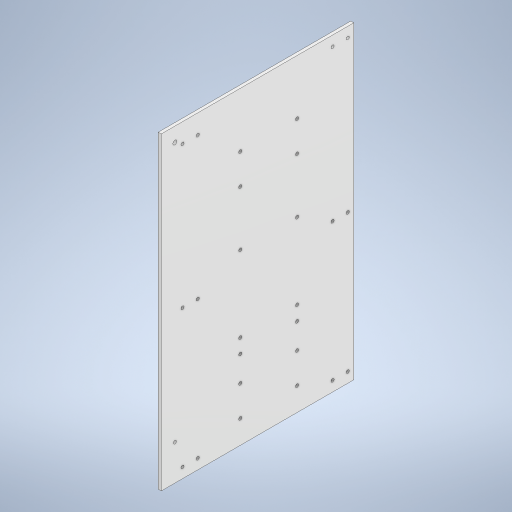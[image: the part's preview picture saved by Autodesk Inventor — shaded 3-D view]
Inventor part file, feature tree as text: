
AUTODESK INVENTOR PART (.ipt)
format: ipt  version: 2024.3 (Build 283343000, 343)  size: 461,824 bytes
history: native  units: mm
features: extrude x17, sketch x17, other x1, projected_geometry x1
ambient origin geometry x8: Origin, YZ Plane, XZ Plane, XY Plane, X Axis, Y Axis, Z Axis, Center Point
bodies: Body1 (feature_tree)
feature tree (36):
  other  "ソリッド1"
  extrude  "押し出し1"  Depth=150.0mm
  extrude  "押し出し2"  Depth=175.0mm
  sketch  "スケッチ3"
  extrude  "押し出し4"  Depth=3.0mm TaperAngle=0.0deg
  extrude  "押し出し5"  Depth=3.0mm
  extrude  "押し出し7"  Depth=6.0mm
  extrude  "押し出し8"  Depth=15.0mm
  extrude  "押し出し9"  Depth=3.0mm
  extrude  "押し出し10"  TaperAngle=0.0deg  [1 undecoded]
  extrude  "押し出し11"  Depth=6.0mm
  extrude  "押し出し12"  Depth=3.0mm
  extrude  "押し出し13"  Depth=15.0mm
  extrude  "押し出し14"  Depth=3.0mm
  extrude  "押し出し15"  Depth=3.0mm
  extrude  "押し出し16"  Depth=3.0mm
  extrude  "押し出し17"  Depth=6.0mm
  extrude  "押し出し18"  Depth=15.0mm
  extrude  "押し出し19"  Depth=5.0mm
  sketch  "スケッチ1"
  sketch  "スケッチ2"
  sketch  "スケッチ6"
  sketch  "スケッチ7"
  sketch  "スケッチ9"
  sketch  "スケッチ10"
  sketch  "スケッチ11"
  sketch  "スケッチ12"
  sketch  "スケッチ13"
  sketch  "スケッチ14"
  sketch  "スケッチ15"
  sketch  "スケッチ16"
  sketch  "スケッチ17"
  sketch  "スケッチ18"
  sketch  "スケッチ19"
  sketch  "スケッチ20"
  projected_geometry  "投影ループ1"
note: 1 required parameter value undecoded (feature->parameter linkage not recoverable at this tier; creation-order binding heuristic only, values carry confidence <= 0.55)
